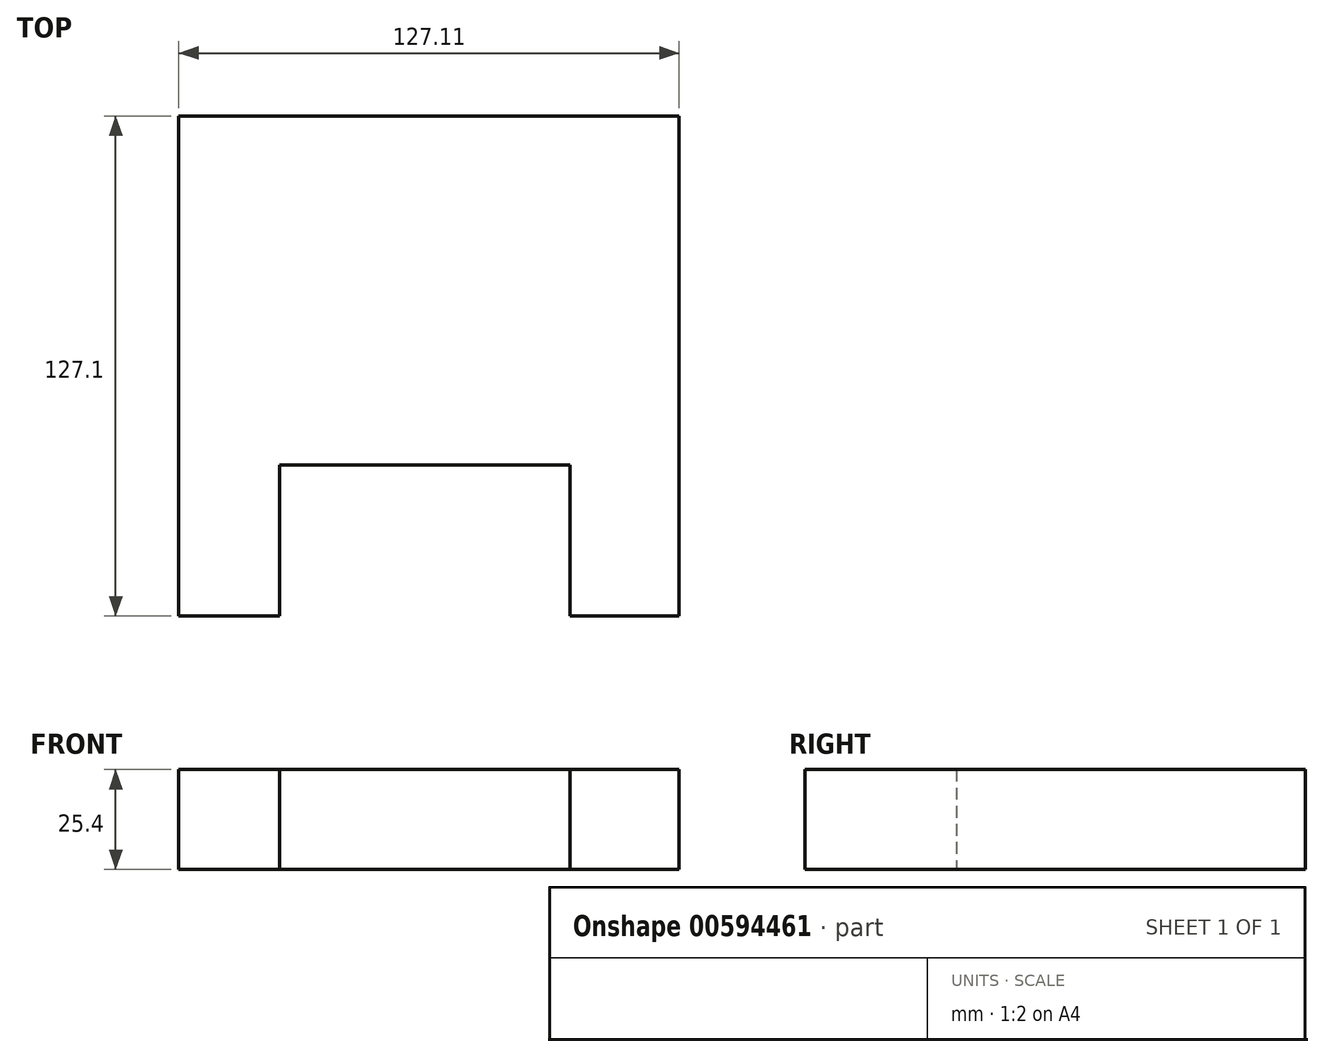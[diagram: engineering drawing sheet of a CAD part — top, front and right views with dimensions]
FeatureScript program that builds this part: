
annotation { "Feature Type Name" : "Feature", "Feature Type Description" : "" }
export const myFeature = defineFeature(function(context is Context, id is Id, definition is map)
    precondition{}
    {
        {
            var Q0;
            Q0=qCreatedBy(makeId("Top.planeOp"),FACE);
            var sketch = newSketch(context, id + "F0", { "sketchPlane" : qUnion([Q0])});
            skLineSegment(sketch, "E0", {"start": v(0, 0) * mm, "end": v(-127.1, 0) * mm});
            skLineSegment(sketch, "E1", {"start": v(-127.1, 0) * mm, "end": v(-127.1, -127.1) * mm});
            skLineSegment(sketch, "E2", {"start": v(-127.1, -127.1) * mm, "end": v(-101.52, -127.1) * mm});
            skLineSegment(sketch, "E3", {"start": v(-101.52, -127.1) * mm, "end": v(-101.52, -88.72) * mm});
            skLineSegment(sketch, "E4", {"start": v(-101.52, -88.72) * mm, "end": v(-27.68, -88.72) * mm});
            skLineSegment(sketch, "E5", {"start": v(-27.68, -88.72) * mm, "end": v(-27.68, -127.1) * mm});
            skLineSegment(sketch, "E6", {"start": v(-27.68, -127.1) * mm, "end": v(0, -127.1) * mm});
            skLineSegment(sketch, "E7", {"start": v(0, -127.1) * mm, "end": v(0, 0) * mm});
            skSolve(sketch);
        }
        {
            var Q0;
            Q0=makeQuery(id+"F0.imprint","IMPRINT",FACE,{"disambiguationData":[TD([[makeQuery(id+"F0.imprint","IMPRINT",EDGE,{"derivedFrom":sQuery(id+"F0.wireOp",EDGE,"E0")}),1.0]])]});
            extrude(context, id + "F1", {"entities" : qUnion([Q0]), "depth" : 25.4 * mm, "offsetDistance" : 25.4 * mm});
        }
    });
